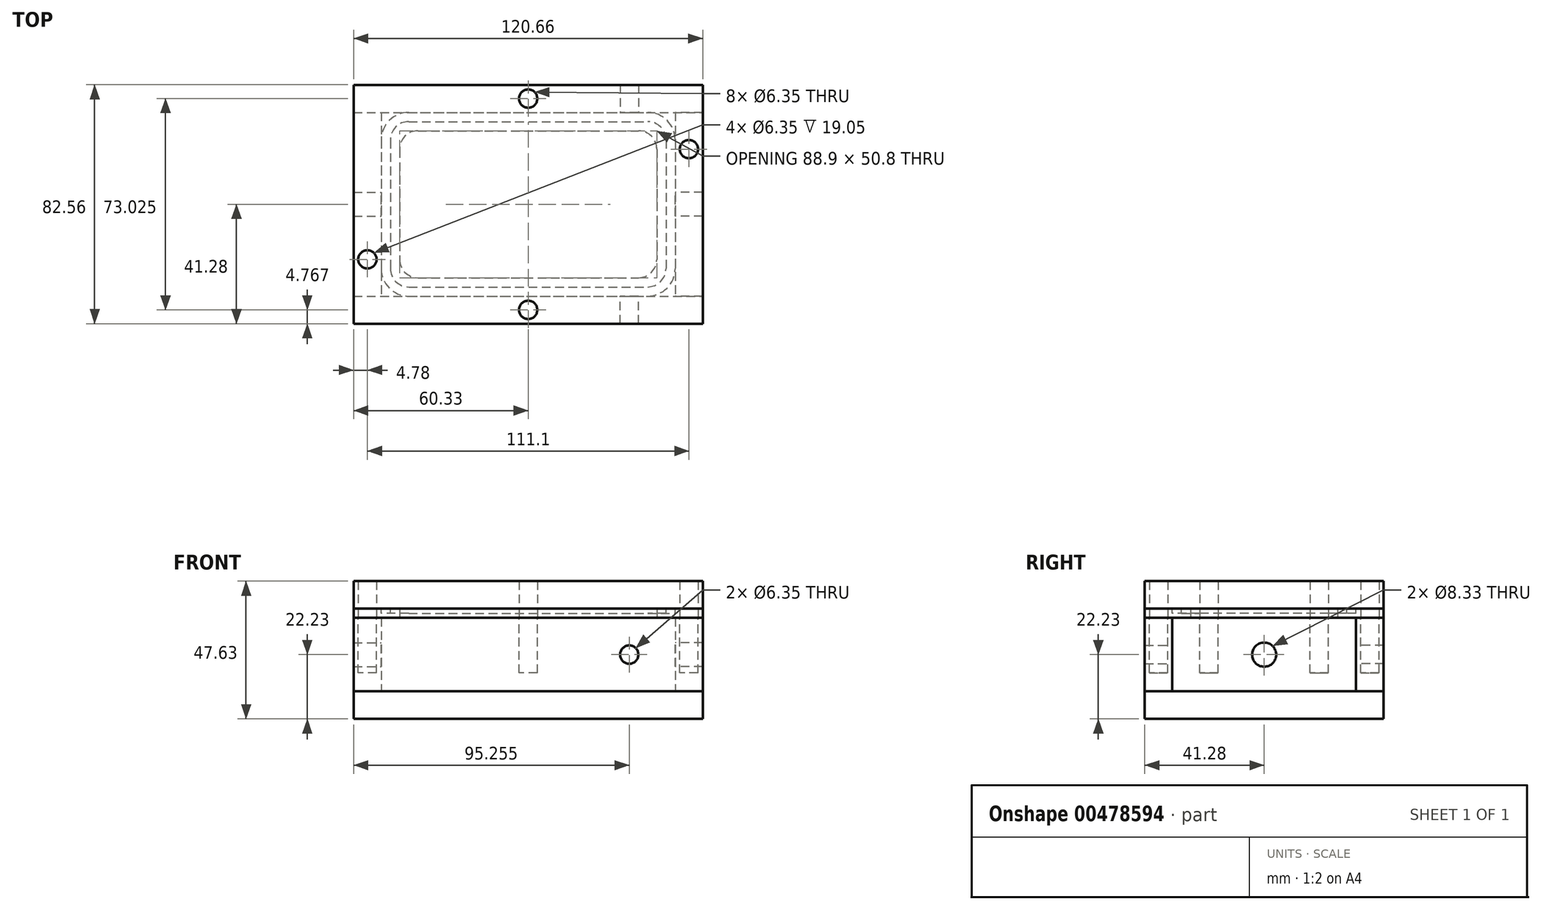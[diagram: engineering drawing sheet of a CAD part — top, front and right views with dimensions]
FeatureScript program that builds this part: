
annotation { "Feature Type Name" : "Feature", "Feature Type Description" : "" }
export const myFeature = defineFeature(function(context is Context, id is Id, definition is map)
    precondition{}
    {
        {
            var Q0;
            Q0=qCreatedBy(makeId("Top.planeOp"),FACE);
            var sketch = newSketch(context, id + "F0", { "sketchPlane" : qUnion([Q0])});
            skLineSegment(sketch, "E0.bottom", {"start": v(-60.33, 31.75) * mm, "end": v(60.33, 31.75) * mm});
            skLineSegment(sketch, "E0.top", {"start": v(-60.33, -31.75) * mm, "end": v(60.32, -31.75) * mm});
            skLineSegment(sketch, "E0.left", {"start": v(-50.8, 31.75) * mm, "end": v(-50.8, -31.75) * mm});
            skLineSegment(sketch, "E0.right", {"start": v(50.8, 31.75) * mm, "end": v(50.8, -31.75) * mm});
            skLineSegment(sketch, "E1", {"start": v(0, -41.27) * mm, "end": v(0, 41.27) * mm, "construction": true});
            skLineSegment(sketch, "E2", {"start": v(-60.33, 0) * mm, "end": v(60.33, 0) * mm, "construction": true});
            skLineSegment(sketch, "E3.0", {"start": v(-60.32, 41.27) * mm, "end": v(60.32, 41.27) * mm});
            skLineSegment(sketch, "E3.1", {"start": v(-60.32, 41.27) * mm, "end": v(-60.33, -41.27) * mm});
            skLineSegment(sketch, "E3.2", {"start": v(-60.32, -41.27) * mm, "end": v(60.32, -41.27) * mm});
            skLineSegment(sketch, "E3.3", {"start": v(60.33, 41.27) * mm, "end": v(60.32, -41.27) * mm});
            skPoint(sketch, "E4.orphan", {"position": v(50.8, 0) * mm});
            skPoint(sketch, "E5.orphan", {"position": v(-50.8, 0) * mm});
            skPoint(sketch, "E6.orphan", {"position": v(0, 31.75) * mm});
            skPoint(sketch, "E7.orphan", {"position": v(0, -31.75) * mm});
            skCircle(sketch, "E8", {"center": v(0, 36.51) * mm, "radius": 3.18 * mm});
            skCircle(sketch, "E9", {"center": v(0, -36.51) * mm, "radius": 3.18 * mm});
            skCircle(sketch, "E10", {"center": v(55.55, 19.05) * mm, "radius": 3.18 * mm});
            skCircle(sketch, "E11", {"center": v(-55.55, -19.05) * mm, "radius": 3.18 * mm});
            skSolve(sketch);
        }
        {
            var Q0;
            Q0=qCreatedBy(makeId("Top.planeOp"),FACE);
            cPlane(context, id + "F1", {"entities" : qUnion([Q0]), "cplaneType" : CPlaneType.OFFSET, "offset" : 12.7 * mm, "width" : 152.4 * mm, "height" : 152.4 * mm});
        }
        {
            var Q0;
            Q0=qCreatedBy(makeId("Top.planeOp"),FACE);
            cPlane(context, id + "F2", {"entities" : qUnion([Q0]), "cplaneType" : CPlaneType.OFFSET, "offset" : 12.7 * mm, "oppositeDirection" : true, "width" : 152.4 * mm, "height" : 152.4 * mm});
        }
        {
            var Q0;
            Q0=qCreatedBy(id+"F2.planeOp",FACE);
            var sketch = newSketch(context, id + "F3", { "sketchPlane" : qUnion([Q0])});
            skLineSegment(sketch, "E12.0", {"start": v(-60.32, 41.27) * mm, "end": v(-60.33, -41.27) * mm});
            skLineSegment(sketch, "E13.0", {"start": v(-60.32, 41.27) * mm, "end": v(60.32, 41.27) * mm});
            skLineSegment(sketch, "E14.0", {"start": v(-60.32, -41.27) * mm, "end": v(60.32, -41.27) * mm});
            skLineSegment(sketch, "E15.0", {"start": v(60.33, 41.27) * mm, "end": v(60.32, -41.27) * mm});
            skSolve(sketch);
        }
        {
            var Q0;
            Q0=qCreatedBy(makeId("Right.planeOp"),FACE);
            cPlane(context, id + "F4", {"entities" : qUnion([Q0]), "cplaneType" : CPlaneType.OFFSET, "offset" : 50.8 * mm, "oppositeDirection" : true, "width" : 152.4 * mm, "height" : 152.4 * mm});
        }
        {
            var Q0;
            Q0=qCreatedBy(id+"F1.planeOp",FACE);
            var sketch = newSketch(context, id + "F5", { "sketchPlane" : qUnion([Q0])});
            skLineSegment(sketch, "E16.0", {"start": v(-60.32, 41.27) * mm, "end": v(-60.33, -41.27) * mm});
            skLineSegment(sketch, "E17.0", {"start": v(-60.32, 41.27) * mm, "end": v(60.32, 41.27) * mm});
            skLineSegment(sketch, "E18.0", {"start": v(-60.32, -41.27) * mm, "end": v(60.32, -41.27) * mm});
            skLineSegment(sketch, "E19.0", {"start": v(60.33, 41.27) * mm, "end": v(60.32, -41.27) * mm});
            skLineSegment(sketch, "E20.0", {"start": v(-50.8, 31.75) * mm, "end": v(50.8, 31.75) * mm});
            skLineSegment(sketch, "E21.0", {"start": v(-50.8, -31.75) * mm, "end": v(50.8, -31.75) * mm});
            skLineSegment(sketch, "E22.0", {"start": v(50.8, 31.75) * mm, "end": v(50.8, -31.75) * mm});
            skLineSegment(sketch, "E23.0", {"start": v(-50.8, 31.75) * mm, "end": v(-50.8, -31.75) * mm});
            skPoint(sketch, "E24.orphan", {"position": v(-60.33, 31.75) * mm});
            skPoint(sketch, "E25.orphan", {"position": v(-60.33, -31.75) * mm});
            skPoint(sketch, "E26.orphan", {"position": v(60.32, -31.75) * mm});
            skPoint(sketch, "E27.orphan", {"position": v(60.33, 31.75) * mm});
            skCircle(sketch, "E28.0", {"center": v(0, 36.51) * mm, "radius": 3.18 * mm});
            skCircle(sketch, "E29.0", {"center": v(-55.55, -19.05) * mm, "radius": 3.18 * mm});
            skLineSegment(sketch, "E30.0", {"start": v(-44.45, 25.4) * mm, "end": v(44.45, 25.4) * mm});
            skLineSegment(sketch, "E30.1", {"start": v(-44.45, 25.4) * mm, "end": v(-44.45, -25.4) * mm});
            skLineSegment(sketch, "E30.2", {"start": v(-44.45, -25.4) * mm, "end": v(44.45, -25.4) * mm});
            skLineSegment(sketch, "E30.3", {"start": v(44.45, 25.4) * mm, "end": v(44.45, -25.4) * mm});
            skLineSegment(sketch, "E31.0", {"start": v(-41.27, 28.57) * mm, "end": v(41.27, 28.57) * mm});
            skLineSegment(sketch, "E31.1", {"start": v(-47.62, 22.23) * mm, "end": v(-47.63, -22.23) * mm});
            skLineSegment(sketch, "E31.2", {"start": v(-41.28, -28.57) * mm, "end": v(41.27, -28.57) * mm});
            skLineSegment(sketch, "E31.3", {"start": v(47.62, 22.23) * mm, "end": v(47.62, -22.23) * mm});
            skPoint(sketch, "E32.visualSharp", {"position": v(-47.62, 28.57) * mm});
            skArc(sketch, "E32.filletArc", {"start": v(-41.27, 28.58) * mm, "mid": v(-45.77, 26.72) * mm, "end": v(-47.62, 22.23) * mm});
            skPoint(sketch, "E33.visualSharp", {"position": v(-47.63, -28.57) * mm});
            skArc(sketch, "E33.filletArc", {"start": v(-47.63, -22.23) * mm, "mid": v(-45.77, -26.72) * mm, "end": v(-41.28, -28.58) * mm});
            skPoint(sketch, "E34.visualSharp", {"position": v(47.62, -28.57) * mm});
            skArc(sketch, "E34.filletArc", {"start": v(41.27, -28.58) * mm, "mid": v(45.77, -26.72) * mm, "end": v(47.62, -22.23) * mm});
            skPoint(sketch, "E35.visualSharp", {"position": v(47.63, 28.57) * mm});
            skArc(sketch, "E35.filletArc", {"start": v(47.62, 22.23) * mm, "mid": v(45.77, 26.72) * mm, "end": v(41.27, 28.58) * mm});
            skLineSegment(sketch, "E36.0", {"start": v(-41.27, 31.75) * mm, "end": v(41.27, 31.75) * mm});
            skArc(sketch, "E36.1", {"start": v(50.8, 22.22) * mm, "mid": v(48.01, 28.96) * mm, "end": v(41.27, 31.75) * mm});
            skArc(sketch, "E36.2", {"start": v(-41.27, 31.75) * mm, "mid": v(-48.01, 28.96) * mm, "end": v(-50.8, 22.23) * mm});
            skLineSegment(sketch, "E36.3", {"start": v(50.8, 22.22) * mm, "end": v(50.8, -22.23) * mm});
            skLineSegment(sketch, "E36.4", {"start": v(-50.8, 22.23) * mm, "end": v(-50.8, -22.22) * mm});
            skArc(sketch, "E36.5", {"start": v(-50.8, -22.22) * mm, "mid": v(-48.01, -28.96) * mm, "end": v(-41.28, -31.75) * mm});
            skLineSegment(sketch, "E36.6", {"start": v(-41.28, -31.75) * mm, "end": v(41.27, -31.75) * mm});
            skArc(sketch, "E36.7", {"start": v(41.27, -31.75) * mm, "mid": v(48.01, -28.96) * mm, "end": v(50.8, -22.23) * mm});
            skSolve(sketch);
        }
        {
            var Q0;
            Q0=qCreatedBy(id+"F4.planeOp",FACE);
            var sketch = newSketch(context, id + "F6", { "sketchPlane" : qUnion([Q0])});
            skLineSegment(sketch, "E37.bottom", {"start": v(31.75, 12.7) * mm, "end": v(-31.75, 12.7) * mm});
            skLineSegment(sketch, "E37.top", {"start": v(31.75, -12.7) * mm, "end": v(-31.75, -12.7) * mm});
            skLineSegment(sketch, "E37.left", {"start": v(31.75, 12.7) * mm, "end": v(31.75, -12.7) * mm});
            skLineSegment(sketch, "E37.right", {"start": v(-31.75, 12.7) * mm, "end": v(-31.75, -12.7) * mm});
            skPoint(sketch, "E38.0", {"position": v(31.75, 0) * mm});
            skCircle(sketch, "E39", {"center": v(0, 0) * mm, "radius": 4.17 * mm});
            skSolve(sketch);
        }
        {
            var Q0;
            Q0=qCreatedBy(makeId("Front.planeOp"),FACE);
            cPlane(context, id + "F7", {"entities" : qUnion([Q0]), "cplaneType" : CPlaneType.OFFSET, "offset" : 31.75 * mm, "width" : 152.4 * mm, "height" : 152.4 * mm});
        }
        {
            var Q0;
            Q0=qCreatedBy(id+"F7.planeOp",FACE);
            var sketch = newSketch(context, id + "F8", { "sketchPlane" : qUnion([Q0])});
            skLineSegment(sketch, "E40.bottom", {"start": v(-60.33, 12.7) * mm, "end": v(60.33, 12.7) * mm});
            skLineSegment(sketch, "E40.top", {"start": v(-60.33, -12.7) * mm, "end": v(60.33, -12.7) * mm});
            skLineSegment(sketch, "E40.left", {"start": v(-60.33, 12.7) * mm, "end": v(-60.33, -12.7) * mm});
            skLineSegment(sketch, "E40.right", {"start": v(60.33, 12.7) * mm, "end": v(60.33, -12.7) * mm});
            skCircle(sketch, "E41", {"center": v(34.92, 0) * mm, "radius": 3.18 * mm});
            skSolve(sketch);
        }
        {
            var Q0;
            Q0=qCreatedBy(id+"F1.planeOp",FACE);
            cPlane(context, id + "F9", {"entities" : qUnion([Q0]), "cplaneType" : CPlaneType.OFFSET, "offset" : 3.17 * mm, "width" : 152.4 * mm, "height" : 152.4 * mm});
        }
        {
            var Q0;
            Q0=qCreatedBy(id+"F2.planeOp",FACE);
            var sketch = newSketch(context, id + "F10", { "sketchPlane" : qUnion([Q0])});
            skLineSegment(sketch, "E42.0", {"start": v(-60.32, -41.27) * mm, "end": v(60.32, -41.27) * mm});
            skLineSegment(sketch, "E43.0", {"start": v(-60.32, 41.27) * mm, "end": v(-60.33, -41.27) * mm});
            skLineSegment(sketch, "E44.0", {"start": v(-60.32, 41.27) * mm, "end": v(60.32, 41.27) * mm});
            skLineSegment(sketch, "E45.0", {"start": v(60.33, 41.27) * mm, "end": v(60.32, -41.27) * mm});
            skSolve(sketch);
        }
        {
            var Q0;
            Q0 = qSketchRegion(id + "F10", true);
            extrude(context, id + "F11", {"entities" : qUnion([Q0]), "oppositeDirection" : true, "depth" : 9.52 * mm});
        }
        {
            var Q0;
            Q0=makeQuery(id+"F6.imprint","IMPRINT",FACE,{"disambiguationData":[TD([[makeQuery(id+"F6.imprint","IMPRINT",EDGE,{"derivedFrom":sQuery(id+"F6.wireOp",EDGE,"E37.bottom")}),1.0]])]});
            extrude(context, id + "F12", {"entities" : qUnion([Q0]), "oppositeDirection" : true, "depth" : 9.52 * mm});
        }
        {
            var Q0;
            Q0=makeQuery(id+"F12.opExtrude","SWEPT_BODY",BODY,{"disambiguationData":[OSD([sQuery(id+"F6.wireOp",EDGE,"E37.bottom"),sQuery(id+"F6.wireOp",EDGE,"E37.top"),sQuery(id+"F6.wireOp",EDGE,"E37.left"),sQuery(id+"F6.wireOp",EDGE,"E37.right"),sQuery(id+"F6.wireOp",EDGE,"E39")])]});
            var Q1;
            Q1=qCreatedBy(makeId("Right.planeOp"),FACE);
            mirror(context, id + "F13", {"entities" : qUnion([Q0]), "mirrorPlane" : qUnion([Q1])});
        }
        {
            var Q0;
            Q0=makeQuery(id+"F8.imprint","IMPRINT",FACE,{"disambiguationData":[TD([[makeQuery(id+"F8.imprint","IMPRINT",EDGE,{"derivedFrom":sQuery(id+"F8.wireOp",EDGE,"E40.bottom")}),-1.0]])]});
            extrude(context, id + "F14", {"entities" : qUnion([Q0]), "depth" : 9.52 * mm});
        }
        {
            var Q0;
            Q0=makeQuery(id+"F14.opExtrude","SWEPT_BODY",BODY,{"disambiguationData":[OSD([sQuery(id+"F8.wireOp",EDGE,"E40.bottom"),sQuery(id+"F8.wireOp",EDGE,"E40.top"),sQuery(id+"F8.wireOp",EDGE,"E40.left"),sQuery(id+"F8.wireOp",EDGE,"E40.right"),sQuery(id+"F8.wireOp",EDGE,"E41")])]});
            var Q1;
            Q1=qCreatedBy(makeId("Front.planeOp"),FACE);
            mirror(context, id + "F15", {"entities" : qUnion([Q0]), "mirrorPlane" : qUnion([Q1])});
        }
        {
            var Q0;
            Q0=qCreatedBy(id+"F1.planeOp",FACE);
            var sketch = newSketch(context, id + "F16", { "sketchPlane" : qUnion([Q0])});
            skLineSegment(sketch, "E46.0", {"start": v(-60.32, 41.27) * mm, "end": v(-60.33, -41.27) * mm});
            skLineSegment(sketch, "E47.0", {"start": v(-60.32, 41.27) * mm, "end": v(60.32, 41.27) * mm});
            skLineSegment(sketch, "E48.0", {"start": v(-60.32, -41.27) * mm, "end": v(60.32, -41.27) * mm});
            skLineSegment(sketch, "E49.0", {"start": v(60.33, 41.27) * mm, "end": v(60.32, -41.27) * mm});
            skLineSegment(sketch, "E50.0", {"start": v(-44.45, 19.05) * mm, "end": v(-44.45, -19.05) * mm});
            skLineSegment(sketch, "E51.0", {"start": v(-38.1, 25.4) * mm, "end": v(38.1, 25.4) * mm});
            skLineSegment(sketch, "E52.0", {"start": v(44.45, 19.05) * mm, "end": v(44.45, -19.05) * mm});
            skLineSegment(sketch, "E53.0", {"start": v(-38.1, -25.4) * mm, "end": v(38.1, -25.4) * mm});
            skCircle(sketch, "E54.0", {"center": v(-55.55, -19.05) * mm, "radius": 3.18 * mm});
            skCircle(sketch, "E55.0", {"center": v(0, 36.51) * mm, "radius": 3.18 * mm});
            skCircle(sketch, "E56.0", {"center": v(55.55, 19.05) * mm, "radius": 3.18 * mm});
            skCircle(sketch, "E57.0", {"center": v(0, -36.51) * mm, "radius": 3.18 * mm});
            skPoint(sketch, "E58.visualSharp", {"position": v(-44.45, 25.4) * mm});
            skArc(sketch, "E58.filletArc", {"start": v(-38.1, 25.4) * mm, "mid": v(-42.6, 23.54) * mm, "end": v(-44.45, 19.05) * mm});
            skPoint(sketch, "E59.visualSharp", {"position": v(-44.45, -25.4) * mm});
            skArc(sketch, "E59.filletArc", {"start": v(-44.45, -19.05) * mm, "mid": v(-42.6, -23.54) * mm, "end": v(-38.1, -25.4) * mm});
            skPoint(sketch, "E60.visualSharp", {"position": v(44.45, -25.4) * mm});
            skArc(sketch, "E60.filletArc", {"start": v(38.1, -25.4) * mm, "mid": v(42.6, -23.54) * mm, "end": v(44.45, -19.05) * mm});
            skPoint(sketch, "E61.visualSharp", {"position": v(44.45, 25.4) * mm});
            skArc(sketch, "E61.filletArc", {"start": v(44.45, 19.05) * mm, "mid": v(42.6, 23.54) * mm, "end": v(38.1, 25.4) * mm});
            skSolve(sketch);
        }
        {
            var Q0;
            Q0 = qSketchRegion(id + "F16", true);
            extrude(context, id + "F17", {"entities" : qUnion([Q0]), "depth" : 3.17 * mm});
        }
        {
            var Q0;
            Q0=qCreatedBy(id+"F9.planeOp",FACE);
            var sketch = newSketch(context, id + "F18", { "sketchPlane" : qUnion([Q0])});
            skArc(sketch, "E62.0", {"start": v(-41.27, 28.58) * mm, "mid": v(-45.77, 26.72) * mm, "end": v(-47.62, 22.23) * mm});
            skLineSegment(sketch, "E63.0", {"start": v(-47.62, 22.23) * mm, "end": v(-47.63, -22.23) * mm});
            skArc(sketch, "E64.0", {"start": v(-47.63, -22.23) * mm, "mid": v(-45.77, -26.72) * mm, "end": v(-41.28, -28.58) * mm});
            skLineSegment(sketch, "E65.0", {"start": v(-41.28, -28.57) * mm, "end": v(41.27, -28.57) * mm});
            skArc(sketch, "E66.0", {"start": v(41.27, -28.58) * mm, "mid": v(45.77, -26.72) * mm, "end": v(47.62, -22.23) * mm});
            skLineSegment(sketch, "E67.0", {"start": v(47.62, 22.23) * mm, "end": v(47.62, -22.23) * mm});
            skLineSegment(sketch, "E68.0", {"start": v(-41.27, 28.57) * mm, "end": v(41.27, 28.57) * mm});
            skArc(sketch, "E69.0", {"start": v(47.62, 22.23) * mm, "mid": v(45.77, 26.72) * mm, "end": v(41.27, 28.58) * mm});
            skLineSegment(sketch, "E70.0", {"start": v(-41.27, 31.75) * mm, "end": v(41.27, 31.75) * mm});
            skArc(sketch, "E70.1", {"start": v(50.8, 22.22) * mm, "mid": v(48.01, 28.96) * mm, "end": v(41.27, 31.75) * mm});
            skArc(sketch, "E70.2", {"start": v(-41.27, 31.75) * mm, "mid": v(-48.01, 28.96) * mm, "end": v(-50.8, 22.22) * mm});
            skLineSegment(sketch, "E70.3", {"start": v(50.8, 22.22) * mm, "end": v(50.8, -22.22) * mm});
            skLineSegment(sketch, "E70.4", {"start": v(-50.8, 22.22) * mm, "end": v(-50.8, -22.22) * mm});
            skArc(sketch, "E70.5", {"start": v(-50.8, -22.22) * mm, "mid": v(-48.01, -28.96) * mm, "end": v(-41.27, -31.75) * mm});
            skLineSegment(sketch, "E70.6", {"start": v(-41.27, -31.75) * mm, "end": v(41.27, -31.75) * mm});
            skArc(sketch, "E70.7", {"start": v(41.27, -31.75) * mm, "mid": v(48.01, -28.96) * mm, "end": v(50.8, -22.22) * mm});
            skSolve(sketch);
        }
        {
            var Q0;
            Q0 = qSketchRegion(id + "F18", true);
            extrude(context, id + "F19", {"entities" : qUnion([Q0]), "operationType" : NewBodyOperationType.REMOVE, "oppositeDirection" : true, "depth" : 1.59 * mm});
        }
        {
            var Q0;
            Q0=qCreatedBy(id+"F9.planeOp",FACE);
            var sketch = newSketch(context, id + "F20", { "sketchPlane" : qUnion([Q0])});
            skLineSegment(sketch, "E71.0", {"start": v(-60.32, 41.27) * mm, "end": v(-60.33, -41.27) * mm});
            skLineSegment(sketch, "E71.1", {"start": v(-60.32, 41.27) * mm, "end": v(60.32, 41.27) * mm});
            skLineSegment(sketch, "E71.2", {"start": v(-60.32, -41.27) * mm, "end": v(60.32, -41.27) * mm});
            skLineSegment(sketch, "E71.3", {"start": v(60.33, 41.27) * mm, "end": v(60.32, -41.27) * mm});
            skCircle(sketch, "E72.0", {"center": v(0, 36.51) * mm, "radius": 3.18 * mm});
            skCircle(sketch, "E72.1", {"center": v(0, -36.51) * mm, "radius": 3.18 * mm});
            skCircle(sketch, "E72.2", {"center": v(55.55, 19.05) * mm, "radius": 3.18 * mm});
            skCircle(sketch, "E72.3", {"center": v(-55.55, -19.05) * mm, "radius": 3.18 * mm});
            skSolve(sketch);
        }
        {
            var Q0;
            Q0 = qSketchRegion(id + "F20", true);
            extrude(context, id + "F21", {"entities" : qUnion([Q0]), "depth" : 9.52 * mm});
        }
        {
            var Q0;
            Q0=qCreatedBy(id+"F1.planeOp",FACE);
            var sketch = newSketch(context, id + "F22", { "sketchPlane" : qUnion([Q0])});
            skCircle(sketch, "E73.0", {"center": v(-55.55, -19.05) * mm, "radius": 3.18 * mm});
            skSolve(sketch);
        }
        {
            var Q0;
            Q0 = qSketchRegion(id + "F22", true);
            extrude(context, id + "F23", {"entities" : qUnion([Q0]), "operationType" : NewBodyOperationType.REMOVE, "oppositeDirection" : true, "depth" : 19.05 * mm});
        }
        {
            var Q0;
            Q0=qCreatedBy(id+"F1.planeOp",FACE);
            var sketch = newSketch(context, id + "F24", { "sketchPlane" : qUnion([Q0])});
            skCircle(sketch, "E74.0", {"center": v(0, -36.51) * mm, "radius": 3.18 * mm});
            skSolve(sketch);
        }
        {
            var Q0;
            Q0 = qSketchRegion(id + "F24", true);
            extrude(context, id + "F25", {"entities" : qUnion([Q0]), "operationType" : NewBodyOperationType.REMOVE, "oppositeDirection" : true, "depth" : 19.05 * mm});
        }
        {
            var Q0;
            Q0=qCreatedBy(id+"F1.planeOp",FACE);
            var sketch = newSketch(context, id + "F26", { "sketchPlane" : qUnion([Q0])});
            skCircle(sketch, "E75.0", {"center": v(55.55, 19.05) * mm, "radius": 3.18 * mm});
            skSolve(sketch);
        }
        {
            var Q0;
            Q0 = qSketchRegion(id + "F26", true);
            extrude(context, id + "F27", {"entities" : qUnion([Q0]), "operationType" : NewBodyOperationType.REMOVE, "oppositeDirection" : true, "depth" : 19.05 * mm});
        }
        {
            var Q0;
            Q0=qCreatedBy(id+"F1.planeOp",FACE);
            var sketch = newSketch(context, id + "F28", { "sketchPlane" : qUnion([Q0])});
            skCircle(sketch, "E76.0", {"center": v(0, 36.51) * mm, "radius": 3.18 * mm});
            skSolve(sketch);
        }
        {
            var Q0;
            Q0 = qSketchRegion(id + "F28", true);
            extrude(context, id + "F29", {"entities" : qUnion([Q0]), "operationType" : NewBodyOperationType.REMOVE, "oppositeDirection" : true, "depth" : 19.05 * mm});
        }
    });
